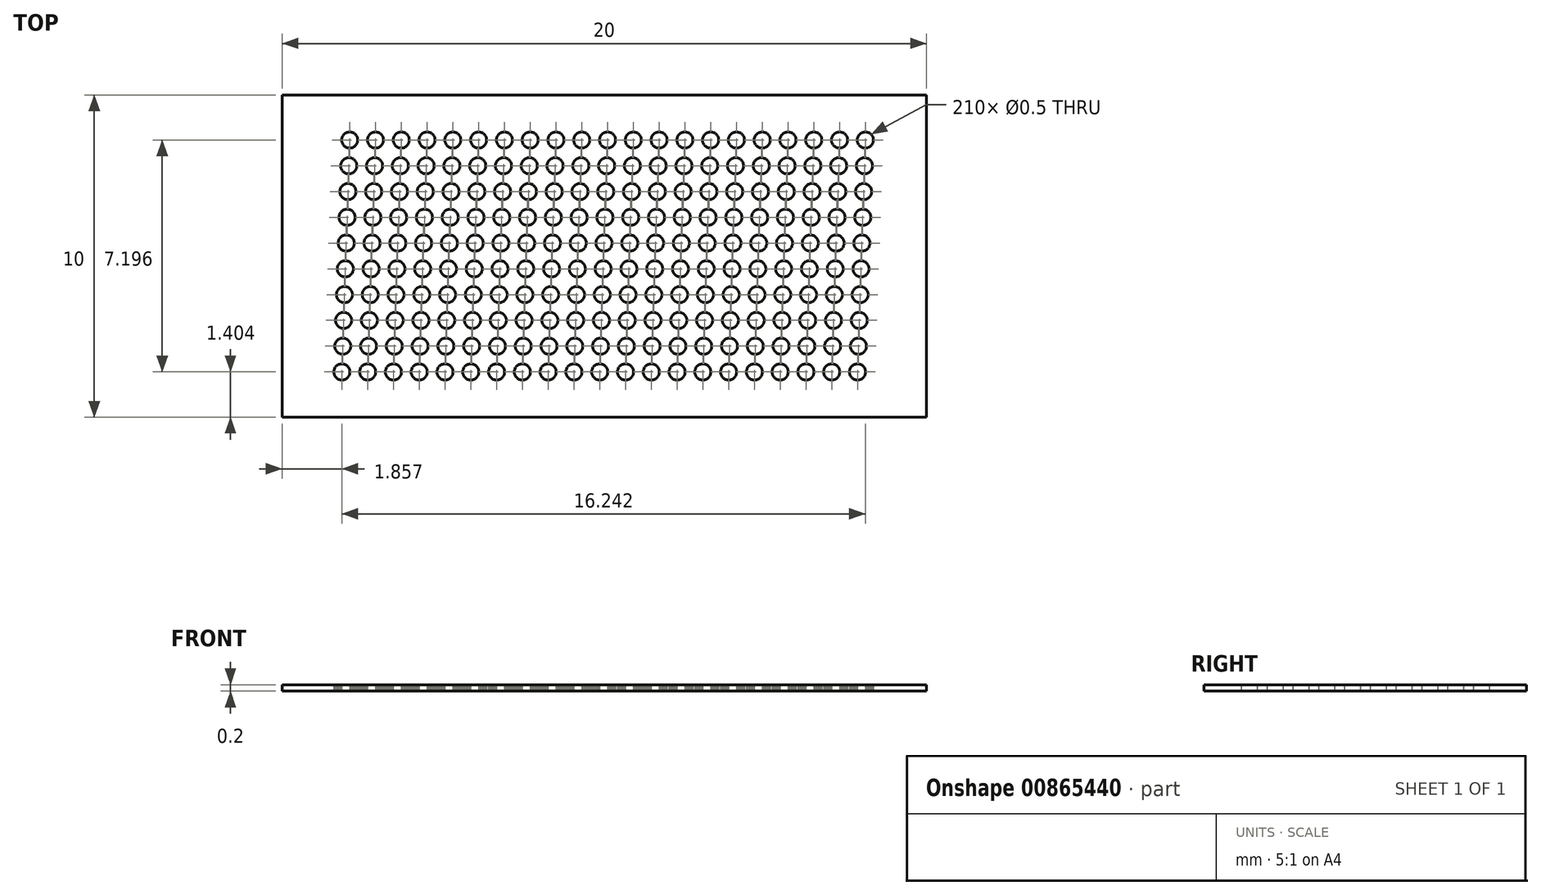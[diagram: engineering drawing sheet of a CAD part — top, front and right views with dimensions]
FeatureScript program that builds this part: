
annotation { "Feature Type Name" : "Feature", "Feature Type Description" : "" }
export const myFeature = defineFeature(function(context is Context, id is Id, definition is map)
    precondition{}
    {
        {
            var Q0;
            Q0=qCreatedBy(makeId("Top.planeOp"),FACE);
            var sketch = newSketch(context, id + "F0", { "sketchPlane" : qUnion([Q0])});
            skLineSegment(sketch, "E0.bottom", {"start": v(0, 0) * mm, "end": v(20, 0) * mm});
            skLineSegment(sketch, "E0.top", {"start": v(0, -10) * mm, "end": v(20, -10) * mm});
            skLineSegment(sketch, "E0.left", {"start": v(0, 0) * mm, "end": v(0, -10) * mm});
            skLineSegment(sketch, "E0.right", {"start": v(20, 0) * mm, "end": v(20, -10) * mm});
            skEllipse(sketch, "E1", {"center": v(2.1, -1.4) * mm, "majorRadius": 0.25 * mm, "minorRadius": 0.25 * mm, "majorAxis": v(0.92, 0.38)});
            skEllipse(sketch, "E2.1.0.0", {"center": v(2.9, -1.4) * mm, "majorRadius": 0.25 * mm, "minorRadius": 0.25 * mm, "majorAxis": v(0.92, 0.38)});
            skEllipse(sketch, "E2.2.0.0", {"center": v(3.7, -1.4) * mm, "majorRadius": 0.25 * mm, "minorRadius": 0.25 * mm, "majorAxis": v(0.92, 0.38)});
            skLineSegment(sketch, "E2.direction1", {"start": v(2.1, -1.4) * mm, "end": v(2.9, -1.4) * mm, "construction": true});
            skEllipse(sketch, "E3.0.3.0", {"center": v(4.5, -1.4) * mm, "majorRadius": 0.25 * mm, "minorRadius": 0.25 * mm, "majorAxis": v(0.92, 0.38)});
            skEllipse(sketch, "E3.0.4.0", {"center": v(5.3, -1.4) * mm, "majorRadius": 0.25 * mm, "minorRadius": 0.25 * mm, "majorAxis": v(0.92, 0.38)});
            skEllipse(sketch, "E3.0.5.0", {"center": v(6.1, -1.4) * mm, "majorRadius": 0.25 * mm, "minorRadius": 0.25 * mm, "majorAxis": v(0.92, 0.38)});
            skEllipse(sketch, "E3.0.6.0", {"center": v(6.9, -1.4) * mm, "majorRadius": 0.25 * mm, "minorRadius": 0.25 * mm, "majorAxis": v(0.92, 0.38)});
            skEllipse(sketch, "E3.0.7.0", {"center": v(7.7, -1.4) * mm, "majorRadius": 0.25 * mm, "minorRadius": 0.25 * mm, "majorAxis": v(0.92, 0.38)});
            skEllipse(sketch, "E3.0.8.0", {"center": v(8.5, -1.4) * mm, "majorRadius": 0.25 * mm, "minorRadius": 0.25 * mm, "majorAxis": v(0.92, 0.38)});
            skEllipse(sketch, "E3.0.9.0", {"center": v(9.3, -1.4) * mm, "majorRadius": 0.25 * mm, "minorRadius": 0.25 * mm, "majorAxis": v(0.92, 0.38)});
            skEllipse(sketch, "E3.0.10.0", {"center": v(10.1, -1.4) * mm, "majorRadius": 0.25 * mm, "minorRadius": 0.25 * mm, "majorAxis": v(0.92, 0.38)});
            skEllipse(sketch, "E3.0.11.0", {"center": v(10.9, -1.4) * mm, "majorRadius": 0.25 * mm, "minorRadius": 0.25 * mm, "majorAxis": v(0.92, 0.38)});
            skEllipse(sketch, "E3.0.12.0", {"center": v(11.7, -1.4) * mm, "majorRadius": 0.25 * mm, "minorRadius": 0.25 * mm, "majorAxis": v(0.92, 0.38)});
            skEllipse(sketch, "E3.0.13.0", {"center": v(12.5, -1.4) * mm, "majorRadius": 0.25 * mm, "minorRadius": 0.25 * mm, "majorAxis": v(0.92, 0.38)});
            skEllipse(sketch, "E3.0.14.0", {"center": v(13.3, -1.4) * mm, "majorRadius": 0.25 * mm, "minorRadius": 0.25 * mm, "majorAxis": v(0.92, 0.38)});
            skEllipse(sketch, "E3.0.15.0", {"center": v(14.1, -1.4) * mm, "majorRadius": 0.25 * mm, "minorRadius": 0.25 * mm, "majorAxis": v(0.92, 0.38)});
            skEllipse(sketch, "E3.0.16.0", {"center": v(14.9, -1.4) * mm, "majorRadius": 0.25 * mm, "minorRadius": 0.25 * mm, "majorAxis": v(0.92, 0.38)});
            skEllipse(sketch, "E3.0.17.0", {"center": v(15.7, -1.4) * mm, "majorRadius": 0.25 * mm, "minorRadius": 0.25 * mm, "majorAxis": v(0.92, 0.38)});
            skEllipse(sketch, "E3.0.18.0", {"center": v(16.5, -1.4) * mm, "majorRadius": 0.25 * mm, "minorRadius": 0.25 * mm, "majorAxis": v(0.92, 0.38)});
            skEllipse(sketch, "E3.0.19.0", {"center": v(17.3, -1.4) * mm, "majorRadius": 0.25 * mm, "minorRadius": 0.25 * mm, "majorAxis": v(0.92, 0.38)});
            skEllipse(sketch, "E4.0.20.0", {"center": v(18.1, -1.4) * mm, "majorRadius": 0.25 * mm, "minorRadius": 0.25 * mm, "majorAxis": v(0.92, 0.38)});
            skEllipse(sketch, "E5.1.0.0", {"center": v(18.07, -2.2) * mm, "majorRadius": 0.25 * mm, "minorRadius": 0.25 * mm, "majorAxis": v(0.92, 0.38)});
            skEllipse(sketch, "E5.1.0.1", {"center": v(17.27, -2.2) * mm, "majorRadius": 0.25 * mm, "minorRadius": 0.25 * mm, "majorAxis": v(0.92, 0.38)});
            skEllipse(sketch, "E5.1.0.2", {"center": v(16.47, -2.2) * mm, "majorRadius": 0.25 * mm, "minorRadius": 0.25 * mm, "majorAxis": v(0.92, 0.38)});
            skEllipse(sketch, "E5.1.0.3", {"center": v(15.67, -2.2) * mm, "majorRadius": 0.25 * mm, "minorRadius": 0.25 * mm, "majorAxis": v(0.92, 0.38)});
            skEllipse(sketch, "E5.1.0.4", {"center": v(14.87, -2.2) * mm, "majorRadius": 0.25 * mm, "minorRadius": 0.25 * mm, "majorAxis": v(0.92, 0.38)});
            skEllipse(sketch, "E5.1.0.5", {"center": v(14.07, -2.2) * mm, "majorRadius": 0.25 * mm, "minorRadius": 0.25 * mm, "majorAxis": v(0.92, 0.38)});
            skEllipse(sketch, "E5.1.0.6", {"center": v(13.27, -2.2) * mm, "majorRadius": 0.25 * mm, "minorRadius": 0.25 * mm, "majorAxis": v(0.92, 0.38)});
            skEllipse(sketch, "E5.1.0.7", {"center": v(12.47, -2.2) * mm, "majorRadius": 0.25 * mm, "minorRadius": 0.25 * mm, "majorAxis": v(0.92, 0.38)});
            skEllipse(sketch, "E5.1.0.8", {"center": v(11.67, -2.2) * mm, "majorRadius": 0.25 * mm, "minorRadius": 0.25 * mm, "majorAxis": v(0.92, 0.38)});
            skEllipse(sketch, "E5.1.0.9", {"center": v(10.87, -2.2) * mm, "majorRadius": 0.25 * mm, "minorRadius": 0.25 * mm, "majorAxis": v(0.92, 0.38)});
            skEllipse(sketch, "E5.1.0.10", {"center": v(10.07, -2.2) * mm, "majorRadius": 0.25 * mm, "minorRadius": 0.25 * mm, "majorAxis": v(0.92, 0.38)});
            skEllipse(sketch, "E5.1.0.11", {"center": v(9.27, -2.2) * mm, "majorRadius": 0.25 * mm, "minorRadius": 0.25 * mm, "majorAxis": v(0.92, 0.38)});
            skEllipse(sketch, "E5.1.0.12", {"center": v(8.47, -2.2) * mm, "majorRadius": 0.25 * mm, "minorRadius": 0.25 * mm, "majorAxis": v(0.92, 0.38)});
            skEllipse(sketch, "E5.1.0.13", {"center": v(7.67, -2.2) * mm, "majorRadius": 0.25 * mm, "minorRadius": 0.25 * mm, "majorAxis": v(0.92, 0.38)});
            skEllipse(sketch, "E5.1.0.14", {"center": v(6.87, -2.2) * mm, "majorRadius": 0.25 * mm, "minorRadius": 0.25 * mm, "majorAxis": v(0.92, 0.38)});
            skEllipse(sketch, "E5.1.0.15", {"center": v(5.27, -2.2) * mm, "majorRadius": 0.25 * mm, "minorRadius": 0.25 * mm, "majorAxis": v(0.92, 0.38)});
            skEllipse(sketch, "E5.1.0.16", {"center": v(4.47, -2.2) * mm, "majorRadius": 0.25 * mm, "minorRadius": 0.25 * mm, "majorAxis": v(0.92, 0.38)});
            skEllipse(sketch, "E5.1.0.17", {"center": v(6.07, -2.2) * mm, "majorRadius": 0.25 * mm, "minorRadius": 0.25 * mm, "majorAxis": v(0.92, 0.38)});
            skEllipse(sketch, "E5.1.0.18", {"center": v(3.67, -2.2) * mm, "majorRadius": 0.25 * mm, "minorRadius": 0.25 * mm, "majorAxis": v(0.92, 0.38)});
            skEllipse(sketch, "E5.1.0.19", {"center": v(2.87, -2.2) * mm, "majorRadius": 0.25 * mm, "minorRadius": 0.25 * mm, "majorAxis": v(0.92, 0.38)});
            skEllipse(sketch, "E5.1.0.20", {"center": v(2.07, -2.2) * mm, "majorRadius": 0.25 * mm, "minorRadius": 0.25 * mm, "majorAxis": v(0.92, 0.38)});
            skEllipse(sketch, "E5.2.0.0", {"center": v(18.05, -3) * mm, "majorRadius": 0.25 * mm, "minorRadius": 0.25 * mm, "majorAxis": v(0.92, 0.38)});
            skEllipse(sketch, "E5.2.0.1", {"center": v(17.25, -3) * mm, "majorRadius": 0.25 * mm, "minorRadius": 0.25 * mm, "majorAxis": v(0.92, 0.38)});
            skEllipse(sketch, "E5.2.0.2", {"center": v(16.45, -3) * mm, "majorRadius": 0.25 * mm, "minorRadius": 0.25 * mm, "majorAxis": v(0.92, 0.38)});
            skEllipse(sketch, "E5.2.0.3", {"center": v(15.65, -3) * mm, "majorRadius": 0.25 * mm, "minorRadius": 0.25 * mm, "majorAxis": v(0.92, 0.38)});
            skEllipse(sketch, "E5.2.0.4", {"center": v(14.85, -3) * mm, "majorRadius": 0.25 * mm, "minorRadius": 0.25 * mm, "majorAxis": v(0.92, 0.38)});
            skEllipse(sketch, "E5.2.0.5", {"center": v(14.05, -3) * mm, "majorRadius": 0.25 * mm, "minorRadius": 0.25 * mm, "majorAxis": v(0.92, 0.38)});
            skEllipse(sketch, "E5.2.0.6", {"center": v(13.25, -3) * mm, "majorRadius": 0.25 * mm, "minorRadius": 0.25 * mm, "majorAxis": v(0.92, 0.38)});
            skEllipse(sketch, "E5.2.0.7", {"center": v(12.45, -3) * mm, "majorRadius": 0.25 * mm, "minorRadius": 0.25 * mm, "majorAxis": v(0.92, 0.38)});
            skEllipse(sketch, "E5.2.0.8", {"center": v(11.65, -3) * mm, "majorRadius": 0.25 * mm, "minorRadius": 0.25 * mm, "majorAxis": v(0.92, 0.38)});
            skEllipse(sketch, "E5.2.0.9", {"center": v(10.85, -3) * mm, "majorRadius": 0.25 * mm, "minorRadius": 0.25 * mm, "majorAxis": v(0.92, 0.38)});
            skEllipse(sketch, "E5.2.0.10", {"center": v(10.05, -3) * mm, "majorRadius": 0.25 * mm, "minorRadius": 0.25 * mm, "majorAxis": v(0.92, 0.38)});
            skEllipse(sketch, "E5.2.0.11", {"center": v(9.25, -3) * mm, "majorRadius": 0.25 * mm, "minorRadius": 0.25 * mm, "majorAxis": v(0.92, 0.38)});
            skEllipse(sketch, "E5.2.0.12", {"center": v(8.45, -3) * mm, "majorRadius": 0.25 * mm, "minorRadius": 0.25 * mm, "majorAxis": v(0.92, 0.38)});
            skEllipse(sketch, "E5.2.0.13", {"center": v(7.65, -3) * mm, "majorRadius": 0.25 * mm, "minorRadius": 0.25 * mm, "majorAxis": v(0.92, 0.38)});
            skEllipse(sketch, "E5.2.0.14", {"center": v(6.85, -3) * mm, "majorRadius": 0.25 * mm, "minorRadius": 0.25 * mm, "majorAxis": v(0.92, 0.38)});
            skEllipse(sketch, "E5.2.0.15", {"center": v(5.25, -3) * mm, "majorRadius": 0.25 * mm, "minorRadius": 0.25 * mm, "majorAxis": v(0.92, 0.38)});
            skEllipse(sketch, "E5.2.0.16", {"center": v(4.45, -3) * mm, "majorRadius": 0.25 * mm, "minorRadius": 0.25 * mm, "majorAxis": v(0.92, 0.38)});
            skEllipse(sketch, "E5.2.0.17", {"center": v(6.05, -3) * mm, "majorRadius": 0.25 * mm, "minorRadius": 0.25 * mm, "majorAxis": v(0.92, 0.38)});
            skEllipse(sketch, "E5.2.0.18", {"center": v(3.65, -3) * mm, "majorRadius": 0.25 * mm, "minorRadius": 0.25 * mm, "majorAxis": v(0.92, 0.38)});
            skEllipse(sketch, "E5.2.0.19", {"center": v(2.85, -3) * mm, "majorRadius": 0.25 * mm, "minorRadius": 0.25 * mm, "majorAxis": v(0.92, 0.38)});
            skEllipse(sketch, "E5.2.0.20", {"center": v(2.05, -3) * mm, "majorRadius": 0.25 * mm, "minorRadius": 0.25 * mm, "majorAxis": v(0.92, 0.38)});
            skEllipse(sketch, "E5.3.0.0", {"center": v(18.02, -3.8) * mm, "majorRadius": 0.25 * mm, "minorRadius": 0.25 * mm, "majorAxis": v(0.92, 0.38)});
            skEllipse(sketch, "E5.3.0.1", {"center": v(17.22, -3.8) * mm, "majorRadius": 0.25 * mm, "minorRadius": 0.25 * mm, "majorAxis": v(0.92, 0.38)});
            skEllipse(sketch, "E5.3.0.2", {"center": v(16.42, -3.8) * mm, "majorRadius": 0.25 * mm, "minorRadius": 0.25 * mm, "majorAxis": v(0.92, 0.38)});
            skEllipse(sketch, "E5.3.0.3", {"center": v(15.62, -3.8) * mm, "majorRadius": 0.25 * mm, "minorRadius": 0.25 * mm, "majorAxis": v(0.92, 0.38)});
            skEllipse(sketch, "E5.3.0.4", {"center": v(14.82, -3.8) * mm, "majorRadius": 0.25 * mm, "minorRadius": 0.25 * mm, "majorAxis": v(0.92, 0.38)});
            skEllipse(sketch, "E5.3.0.5", {"center": v(14.02, -3.8) * mm, "majorRadius": 0.25 * mm, "minorRadius": 0.25 * mm, "majorAxis": v(0.92, 0.38)});
            skEllipse(sketch, "E5.3.0.6", {"center": v(13.22, -3.8) * mm, "majorRadius": 0.25 * mm, "minorRadius": 0.25 * mm, "majorAxis": v(0.92, 0.38)});
            skEllipse(sketch, "E5.3.0.7", {"center": v(12.42, -3.8) * mm, "majorRadius": 0.25 * mm, "minorRadius": 0.25 * mm, "majorAxis": v(0.92, 0.38)});
            skEllipse(sketch, "E5.3.0.8", {"center": v(11.62, -3.8) * mm, "majorRadius": 0.25 * mm, "minorRadius": 0.25 * mm, "majorAxis": v(0.92, 0.38)});
            skEllipse(sketch, "E5.3.0.9", {"center": v(10.82, -3.8) * mm, "majorRadius": 0.25 * mm, "minorRadius": 0.25 * mm, "majorAxis": v(0.92, 0.38)});
            skEllipse(sketch, "E5.3.0.10", {"center": v(10.02, -3.8) * mm, "majorRadius": 0.25 * mm, "minorRadius": 0.25 * mm, "majorAxis": v(0.92, 0.38)});
            skEllipse(sketch, "E5.3.0.11", {"center": v(9.22, -3.8) * mm, "majorRadius": 0.25 * mm, "minorRadius": 0.25 * mm, "majorAxis": v(0.92, 0.38)});
            skEllipse(sketch, "E5.3.0.12", {"center": v(8.42, -3.8) * mm, "majorRadius": 0.25 * mm, "minorRadius": 0.25 * mm, "majorAxis": v(0.92, 0.38)});
            skEllipse(sketch, "E5.3.0.13", {"center": v(7.62, -3.8) * mm, "majorRadius": 0.25 * mm, "minorRadius": 0.25 * mm, "majorAxis": v(0.92, 0.38)});
            skEllipse(sketch, "E5.3.0.14", {"center": v(6.82, -3.8) * mm, "majorRadius": 0.25 * mm, "minorRadius": 0.25 * mm, "majorAxis": v(0.92, 0.38)});
            skEllipse(sketch, "E5.3.0.15", {"center": v(5.22, -3.8) * mm, "majorRadius": 0.25 * mm, "minorRadius": 0.25 * mm, "majorAxis": v(0.92, 0.38)});
            skEllipse(sketch, "E5.3.0.16", {"center": v(4.42, -3.8) * mm, "majorRadius": 0.25 * mm, "minorRadius": 0.25 * mm, "majorAxis": v(0.92, 0.38)});
            skEllipse(sketch, "E5.3.0.17", {"center": v(6.02, -3.8) * mm, "majorRadius": 0.25 * mm, "minorRadius": 0.25 * mm, "majorAxis": v(0.92, 0.38)});
            skEllipse(sketch, "E5.3.0.18", {"center": v(3.62, -3.8) * mm, "majorRadius": 0.25 * mm, "minorRadius": 0.25 * mm, "majorAxis": v(0.92, 0.38)});
            skEllipse(sketch, "E5.3.0.19", {"center": v(2.82, -3.8) * mm, "majorRadius": 0.25 * mm, "minorRadius": 0.25 * mm, "majorAxis": v(0.92, 0.38)});
            skEllipse(sketch, "E5.3.0.20", {"center": v(2.02, -3.8) * mm, "majorRadius": 0.25 * mm, "minorRadius": 0.25 * mm, "majorAxis": v(0.92, 0.38)});
            skEllipse(sketch, "E5.4.0.0", {"center": v(18, -4.6) * mm, "majorRadius": 0.25 * mm, "minorRadius": 0.25 * mm, "majorAxis": v(0.92, 0.38)});
            skEllipse(sketch, "E5.4.0.1", {"center": v(17.2, -4.6) * mm, "majorRadius": 0.25 * mm, "minorRadius": 0.25 * mm, "majorAxis": v(0.92, 0.38)});
            skEllipse(sketch, "E5.4.0.2", {"center": v(16.4, -4.6) * mm, "majorRadius": 0.25 * mm, "minorRadius": 0.25 * mm, "majorAxis": v(0.92, 0.38)});
            skEllipse(sketch, "E5.4.0.3", {"center": v(15.6, -4.6) * mm, "majorRadius": 0.25 * mm, "minorRadius": 0.25 * mm, "majorAxis": v(0.92, 0.38)});
            skEllipse(sketch, "E5.4.0.4", {"center": v(14.8, -4.6) * mm, "majorRadius": 0.25 * mm, "minorRadius": 0.25 * mm, "majorAxis": v(0.92, 0.38)});
            skEllipse(sketch, "E5.4.0.5", {"center": v(14, -4.6) * mm, "majorRadius": 0.25 * mm, "minorRadius": 0.25 * mm, "majorAxis": v(0.92, 0.38)});
            skEllipse(sketch, "E5.4.0.6", {"center": v(13.2, -4.6) * mm, "majorRadius": 0.25 * mm, "minorRadius": 0.25 * mm, "majorAxis": v(0.92, 0.38)});
            skEllipse(sketch, "E5.4.0.7", {"center": v(12.4, -4.6) * mm, "majorRadius": 0.25 * mm, "minorRadius": 0.25 * mm, "majorAxis": v(0.92, 0.38)});
            skEllipse(sketch, "E5.4.0.8", {"center": v(11.6, -4.6) * mm, "majorRadius": 0.25 * mm, "minorRadius": 0.25 * mm, "majorAxis": v(0.92, 0.38)});
            skEllipse(sketch, "E5.4.0.9", {"center": v(10.8, -4.6) * mm, "majorRadius": 0.25 * mm, "minorRadius": 0.25 * mm, "majorAxis": v(0.92, 0.38)});
            skEllipse(sketch, "E5.4.0.10", {"center": v(10, -4.6) * mm, "majorRadius": 0.25 * mm, "minorRadius": 0.25 * mm, "majorAxis": v(0.92, 0.38)});
            skEllipse(sketch, "E5.4.0.11", {"center": v(9.2, -4.6) * mm, "majorRadius": 0.25 * mm, "minorRadius": 0.25 * mm, "majorAxis": v(0.92, 0.38)});
            skEllipse(sketch, "E5.4.0.12", {"center": v(8.4, -4.6) * mm, "majorRadius": 0.25 * mm, "minorRadius": 0.25 * mm, "majorAxis": v(0.92, 0.38)});
            skEllipse(sketch, "E5.4.0.13", {"center": v(7.6, -4.6) * mm, "majorRadius": 0.25 * mm, "minorRadius": 0.25 * mm, "majorAxis": v(0.92, 0.38)});
            skEllipse(sketch, "E5.4.0.14", {"center": v(6.8, -4.6) * mm, "majorRadius": 0.25 * mm, "minorRadius": 0.25 * mm, "majorAxis": v(0.92, 0.38)});
            skEllipse(sketch, "E5.4.0.15", {"center": v(5.2, -4.6) * mm, "majorRadius": 0.25 * mm, "minorRadius": 0.25 * mm, "majorAxis": v(0.92, 0.38)});
            skEllipse(sketch, "E5.4.0.16", {"center": v(4.4, -4.6) * mm, "majorRadius": 0.25 * mm, "minorRadius": 0.25 * mm, "majorAxis": v(0.92, 0.38)});
            skEllipse(sketch, "E5.4.0.17", {"center": v(6, -4.6) * mm, "majorRadius": 0.25 * mm, "minorRadius": 0.25 * mm, "majorAxis": v(0.92, 0.38)});
            skEllipse(sketch, "E5.4.0.18", {"center": v(3.6, -4.6) * mm, "majorRadius": 0.25 * mm, "minorRadius": 0.25 * mm, "majorAxis": v(0.92, 0.38)});
            skEllipse(sketch, "E5.4.0.19", {"center": v(2.8, -4.6) * mm, "majorRadius": 0.25 * mm, "minorRadius": 0.25 * mm, "majorAxis": v(0.92, 0.38)});
            skEllipse(sketch, "E5.4.0.20", {"center": v(2, -4.6) * mm, "majorRadius": 0.25 * mm, "minorRadius": 0.25 * mm, "majorAxis": v(0.92, 0.38)});
            skEllipse(sketch, "E5.5.0.0", {"center": v(17.97, -5.4) * mm, "majorRadius": 0.25 * mm, "minorRadius": 0.25 * mm, "majorAxis": v(0.92, 0.38)});
            skEllipse(sketch, "E5.5.0.1", {"center": v(17.17, -5.4) * mm, "majorRadius": 0.25 * mm, "minorRadius": 0.25 * mm, "majorAxis": v(0.92, 0.38)});
            skEllipse(sketch, "E5.5.0.2", {"center": v(16.37, -5.4) * mm, "majorRadius": 0.25 * mm, "minorRadius": 0.25 * mm, "majorAxis": v(0.92, 0.38)});
            skEllipse(sketch, "E5.5.0.3", {"center": v(15.57, -5.4) * mm, "majorRadius": 0.25 * mm, "minorRadius": 0.25 * mm, "majorAxis": v(0.92, 0.38)});
            skEllipse(sketch, "E5.5.0.4", {"center": v(14.77, -5.4) * mm, "majorRadius": 0.25 * mm, "minorRadius": 0.25 * mm, "majorAxis": v(0.92, 0.38)});
            skEllipse(sketch, "E5.5.0.5", {"center": v(13.97, -5.4) * mm, "majorRadius": 0.25 * mm, "minorRadius": 0.25 * mm, "majorAxis": v(0.92, 0.38)});
            skEllipse(sketch, "E5.5.0.6", {"center": v(13.17, -5.4) * mm, "majorRadius": 0.25 * mm, "minorRadius": 0.25 * mm, "majorAxis": v(0.92, 0.38)});
            skEllipse(sketch, "E5.5.0.7", {"center": v(12.37, -5.4) * mm, "majorRadius": 0.25 * mm, "minorRadius": 0.25 * mm, "majorAxis": v(0.92, 0.38)});
            skEllipse(sketch, "E5.5.0.8", {"center": v(11.57, -5.4) * mm, "majorRadius": 0.25 * mm, "minorRadius": 0.25 * mm, "majorAxis": v(0.92, 0.38)});
            skEllipse(sketch, "E5.5.0.9", {"center": v(10.77, -5.4) * mm, "majorRadius": 0.25 * mm, "minorRadius": 0.25 * mm, "majorAxis": v(0.92, 0.38)});
            skEllipse(sketch, "E5.5.0.10", {"center": v(9.97, -5.4) * mm, "majorRadius": 0.25 * mm, "minorRadius": 0.25 * mm, "majorAxis": v(0.92, 0.38)});
            skEllipse(sketch, "E5.5.0.11", {"center": v(9.17, -5.4) * mm, "majorRadius": 0.25 * mm, "minorRadius": 0.25 * mm, "majorAxis": v(0.92, 0.38)});
            skEllipse(sketch, "E5.5.0.12", {"center": v(8.37, -5.4) * mm, "majorRadius": 0.25 * mm, "minorRadius": 0.25 * mm, "majorAxis": v(0.92, 0.38)});
            skEllipse(sketch, "E5.5.0.13", {"center": v(7.57, -5.4) * mm, "majorRadius": 0.25 * mm, "minorRadius": 0.25 * mm, "majorAxis": v(0.92, 0.38)});
            skEllipse(sketch, "E5.5.0.14", {"center": v(6.77, -5.4) * mm, "majorRadius": 0.25 * mm, "minorRadius": 0.25 * mm, "majorAxis": v(0.92, 0.38)});
            skEllipse(sketch, "E5.5.0.15", {"center": v(5.17, -5.4) * mm, "majorRadius": 0.25 * mm, "minorRadius": 0.25 * mm, "majorAxis": v(0.92, 0.38)});
            skEllipse(sketch, "E5.5.0.16", {"center": v(4.37, -5.4) * mm, "majorRadius": 0.25 * mm, "minorRadius": 0.25 * mm, "majorAxis": v(0.92, 0.38)});
            skEllipse(sketch, "E5.5.0.17", {"center": v(5.97, -5.4) * mm, "majorRadius": 0.25 * mm, "minorRadius": 0.25 * mm, "majorAxis": v(0.92, 0.38)});
            skEllipse(sketch, "E5.5.0.18", {"center": v(3.57, -5.4) * mm, "majorRadius": 0.25 * mm, "minorRadius": 0.25 * mm, "majorAxis": v(0.92, 0.38)});
            skEllipse(sketch, "E5.5.0.19", {"center": v(2.77, -5.4) * mm, "majorRadius": 0.25 * mm, "minorRadius": 0.25 * mm, "majorAxis": v(0.92, 0.38)});
            skEllipse(sketch, "E5.5.0.20", {"center": v(1.97, -5.4) * mm, "majorRadius": 0.25 * mm, "minorRadius": 0.25 * mm, "majorAxis": v(0.92, 0.38)});
            skEllipse(sketch, "E5.6.0.0", {"center": v(17.94, -6.2) * mm, "majorRadius": 0.25 * mm, "minorRadius": 0.25 * mm, "majorAxis": v(0.92, 0.38)});
            skEllipse(sketch, "E5.6.0.1", {"center": v(17.14, -6.2) * mm, "majorRadius": 0.25 * mm, "minorRadius": 0.25 * mm, "majorAxis": v(0.92, 0.38)});
            skEllipse(sketch, "E5.6.0.2", {"center": v(16.34, -6.2) * mm, "majorRadius": 0.25 * mm, "minorRadius": 0.25 * mm, "majorAxis": v(0.92, 0.38)});
            skEllipse(sketch, "E5.6.0.3", {"center": v(15.54, -6.2) * mm, "majorRadius": 0.25 * mm, "minorRadius": 0.25 * mm, "majorAxis": v(0.92, 0.38)});
            skEllipse(sketch, "E5.6.0.4", {"center": v(14.74, -6.2) * mm, "majorRadius": 0.25 * mm, "minorRadius": 0.25 * mm, "majorAxis": v(0.92, 0.38)});
            skEllipse(sketch, "E5.6.0.5", {"center": v(13.94, -6.2) * mm, "majorRadius": 0.25 * mm, "minorRadius": 0.25 * mm, "majorAxis": v(0.92, 0.38)});
            skEllipse(sketch, "E5.6.0.6", {"center": v(13.14, -6.2) * mm, "majorRadius": 0.25 * mm, "minorRadius": 0.25 * mm, "majorAxis": v(0.92, 0.38)});
            skEllipse(sketch, "E5.6.0.7", {"center": v(12.34, -6.2) * mm, "majorRadius": 0.25 * mm, "minorRadius": 0.25 * mm, "majorAxis": v(0.92, 0.38)});
            skEllipse(sketch, "E5.6.0.8", {"center": v(11.54, -6.2) * mm, "majorRadius": 0.25 * mm, "minorRadius": 0.25 * mm, "majorAxis": v(0.92, 0.38)});
            skEllipse(sketch, "E5.6.0.9", {"center": v(10.74, -6.2) * mm, "majorRadius": 0.25 * mm, "minorRadius": 0.25 * mm, "majorAxis": v(0.92, 0.38)});
            skEllipse(sketch, "E5.6.0.10", {"center": v(9.94, -6.2) * mm, "majorRadius": 0.25 * mm, "minorRadius": 0.25 * mm, "majorAxis": v(0.92, 0.38)});
            skEllipse(sketch, "E5.6.0.11", {"center": v(9.14, -6.2) * mm, "majorRadius": 0.25 * mm, "minorRadius": 0.25 * mm, "majorAxis": v(0.92, 0.38)});
            skEllipse(sketch, "E5.6.0.12", {"center": v(8.34, -6.2) * mm, "majorRadius": 0.25 * mm, "minorRadius": 0.25 * mm, "majorAxis": v(0.92, 0.38)});
            skEllipse(sketch, "E5.6.0.13", {"center": v(7.54, -6.2) * mm, "majorRadius": 0.25 * mm, "minorRadius": 0.25 * mm, "majorAxis": v(0.92, 0.38)});
            skEllipse(sketch, "E5.6.0.14", {"center": v(6.74, -6.2) * mm, "majorRadius": 0.25 * mm, "minorRadius": 0.25 * mm, "majorAxis": v(0.92, 0.38)});
            skEllipse(sketch, "E5.6.0.15", {"center": v(5.14, -6.2) * mm, "majorRadius": 0.25 * mm, "minorRadius": 0.25 * mm, "majorAxis": v(0.92, 0.38)});
            skEllipse(sketch, "E5.6.0.16", {"center": v(4.34, -6.2) * mm, "majorRadius": 0.25 * mm, "minorRadius": 0.25 * mm, "majorAxis": v(0.92, 0.38)});
            skEllipse(sketch, "E5.6.0.17", {"center": v(5.94, -6.2) * mm, "majorRadius": 0.25 * mm, "minorRadius": 0.25 * mm, "majorAxis": v(0.92, 0.38)});
            skEllipse(sketch, "E5.6.0.18", {"center": v(3.54, -6.2) * mm, "majorRadius": 0.25 * mm, "minorRadius": 0.25 * mm, "majorAxis": v(0.92, 0.38)});
            skEllipse(sketch, "E5.6.0.19", {"center": v(2.74, -6.2) * mm, "majorRadius": 0.25 * mm, "minorRadius": 0.25 * mm, "majorAxis": v(0.92, 0.38)});
            skEllipse(sketch, "E5.6.0.20", {"center": v(1.94, -6.2) * mm, "majorRadius": 0.25 * mm, "minorRadius": 0.25 * mm, "majorAxis": v(0.92, 0.38)});
            skEllipse(sketch, "E5.7.0.0", {"center": v(17.91, -7) * mm, "majorRadius": 0.25 * mm, "minorRadius": 0.25 * mm, "majorAxis": v(0.92, 0.38)});
            skEllipse(sketch, "E5.7.0.1", {"center": v(17.11, -7) * mm, "majorRadius": 0.25 * mm, "minorRadius": 0.25 * mm, "majorAxis": v(0.92, 0.38)});
            skEllipse(sketch, "E5.7.0.2", {"center": v(16.31, -7) * mm, "majorRadius": 0.25 * mm, "minorRadius": 0.25 * mm, "majorAxis": v(0.92, 0.38)});
            skEllipse(sketch, "E5.7.0.3", {"center": v(15.51, -7) * mm, "majorRadius": 0.25 * mm, "minorRadius": 0.25 * mm, "majorAxis": v(0.92, 0.38)});
            skEllipse(sketch, "E5.7.0.4", {"center": v(14.71, -7) * mm, "majorRadius": 0.25 * mm, "minorRadius": 0.25 * mm, "majorAxis": v(0.92, 0.38)});
            skEllipse(sketch, "E5.7.0.5", {"center": v(13.91, -7) * mm, "majorRadius": 0.25 * mm, "minorRadius": 0.25 * mm, "majorAxis": v(0.92, 0.38)});
            skEllipse(sketch, "E5.7.0.6", {"center": v(13.11, -7) * mm, "majorRadius": 0.25 * mm, "minorRadius": 0.25 * mm, "majorAxis": v(0.92, 0.38)});
            skEllipse(sketch, "E5.7.0.7", {"center": v(12.31, -7) * mm, "majorRadius": 0.25 * mm, "minorRadius": 0.25 * mm, "majorAxis": v(0.92, 0.38)});
            skEllipse(sketch, "E5.7.0.8", {"center": v(11.51, -7) * mm, "majorRadius": 0.25 * mm, "minorRadius": 0.25 * mm, "majorAxis": v(0.92, 0.38)});
            skEllipse(sketch, "E5.7.0.9", {"center": v(10.71, -7) * mm, "majorRadius": 0.25 * mm, "minorRadius": 0.25 * mm, "majorAxis": v(0.92, 0.38)});
            skEllipse(sketch, "E5.7.0.10", {"center": v(9.91, -7) * mm, "majorRadius": 0.25 * mm, "minorRadius": 0.25 * mm, "majorAxis": v(0.92, 0.38)});
            skEllipse(sketch, "E5.7.0.11", {"center": v(9.11, -7) * mm, "majorRadius": 0.25 * mm, "minorRadius": 0.25 * mm, "majorAxis": v(0.92, 0.38)});
            skEllipse(sketch, "E5.7.0.12", {"center": v(8.31, -7) * mm, "majorRadius": 0.25 * mm, "minorRadius": 0.25 * mm, "majorAxis": v(0.92, 0.38)});
            skEllipse(sketch, "E5.7.0.13", {"center": v(7.51, -7) * mm, "majorRadius": 0.25 * mm, "minorRadius": 0.25 * mm, "majorAxis": v(0.92, 0.38)});
            skEllipse(sketch, "E5.7.0.14", {"center": v(6.71, -7) * mm, "majorRadius": 0.25 * mm, "minorRadius": 0.25 * mm, "majorAxis": v(0.92, 0.38)});
            skEllipse(sketch, "E5.7.0.15", {"center": v(5.11, -7) * mm, "majorRadius": 0.25 * mm, "minorRadius": 0.25 * mm, "majorAxis": v(0.92, 0.38)});
            skEllipse(sketch, "E5.7.0.16", {"center": v(4.31, -7) * mm, "majorRadius": 0.25 * mm, "minorRadius": 0.25 * mm, "majorAxis": v(0.92, 0.38)});
            skEllipse(sketch, "E5.7.0.17", {"center": v(5.91, -7) * mm, "majorRadius": 0.25 * mm, "minorRadius": 0.25 * mm, "majorAxis": v(0.92, 0.38)});
            skEllipse(sketch, "E5.7.0.18", {"center": v(3.51, -7) * mm, "majorRadius": 0.25 * mm, "minorRadius": 0.25 * mm, "majorAxis": v(0.92, 0.38)});
            skEllipse(sketch, "E5.7.0.19", {"center": v(2.71, -7) * mm, "majorRadius": 0.25 * mm, "minorRadius": 0.25 * mm, "majorAxis": v(0.92, 0.38)});
            skEllipse(sketch, "E5.7.0.20", {"center": v(1.91, -7) * mm, "majorRadius": 0.25 * mm, "minorRadius": 0.25 * mm, "majorAxis": v(0.92, 0.38)});
            skEllipse(sketch, "E5.8.0.0", {"center": v(17.88, -7.8) * mm, "majorRadius": 0.25 * mm, "minorRadius": 0.25 * mm, "majorAxis": v(0.92, 0.38)});
            skEllipse(sketch, "E5.8.0.1", {"center": v(17.08, -7.8) * mm, "majorRadius": 0.25 * mm, "minorRadius": 0.25 * mm, "majorAxis": v(0.92, 0.38)});
            skEllipse(sketch, "E5.8.0.2", {"center": v(16.28, -7.8) * mm, "majorRadius": 0.25 * mm, "minorRadius": 0.25 * mm, "majorAxis": v(0.92, 0.38)});
            skEllipse(sketch, "E5.8.0.3", {"center": v(15.48, -7.8) * mm, "majorRadius": 0.25 * mm, "minorRadius": 0.25 * mm, "majorAxis": v(0.92, 0.38)});
            skEllipse(sketch, "E5.8.0.4", {"center": v(14.68, -7.8) * mm, "majorRadius": 0.25 * mm, "minorRadius": 0.25 * mm, "majorAxis": v(0.92, 0.38)});
            skEllipse(sketch, "E5.8.0.5", {"center": v(13.88, -7.8) * mm, "majorRadius": 0.25 * mm, "minorRadius": 0.25 * mm, "majorAxis": v(0.92, 0.38)});
            skEllipse(sketch, "E5.8.0.6", {"center": v(13.08, -7.8) * mm, "majorRadius": 0.25 * mm, "minorRadius": 0.25 * mm, "majorAxis": v(0.92, 0.38)});
            skEllipse(sketch, "E5.8.0.7", {"center": v(12.28, -7.8) * mm, "majorRadius": 0.25 * mm, "minorRadius": 0.25 * mm, "majorAxis": v(0.92, 0.38)});
            skEllipse(sketch, "E5.8.0.8", {"center": v(11.48, -7.8) * mm, "majorRadius": 0.25 * mm, "minorRadius": 0.25 * mm, "majorAxis": v(0.92, 0.38)});
            skEllipse(sketch, "E5.8.0.9", {"center": v(10.68, -7.8) * mm, "majorRadius": 0.25 * mm, "minorRadius": 0.25 * mm, "majorAxis": v(0.92, 0.38)});
            skEllipse(sketch, "E5.8.0.10", {"center": v(9.88, -7.8) * mm, "majorRadius": 0.25 * mm, "minorRadius": 0.25 * mm, "majorAxis": v(0.92, 0.38)});
            skEllipse(sketch, "E5.8.0.11", {"center": v(9.08, -7.8) * mm, "majorRadius": 0.25 * mm, "minorRadius": 0.25 * mm, "majorAxis": v(0.92, 0.38)});
            skEllipse(sketch, "E5.8.0.12", {"center": v(8.28, -7.8) * mm, "majorRadius": 0.25 * mm, "minorRadius": 0.25 * mm, "majorAxis": v(0.92, 0.38)});
            skEllipse(sketch, "E5.8.0.13", {"center": v(7.48, -7.8) * mm, "majorRadius": 0.25 * mm, "minorRadius": 0.25 * mm, "majorAxis": v(0.92, 0.38)});
            skEllipse(sketch, "E5.8.0.14", {"center": v(6.68, -7.8) * mm, "majorRadius": 0.25 * mm, "minorRadius": 0.25 * mm, "majorAxis": v(0.92, 0.38)});
            skEllipse(sketch, "E5.8.0.15", {"center": v(5.08, -7.8) * mm, "majorRadius": 0.25 * mm, "minorRadius": 0.25 * mm, "majorAxis": v(0.92, 0.38)});
            skEllipse(sketch, "E5.8.0.16", {"center": v(4.28, -7.8) * mm, "majorRadius": 0.25 * mm, "minorRadius": 0.25 * mm, "majorAxis": v(0.92, 0.38)});
            skEllipse(sketch, "E5.8.0.17", {"center": v(5.88, -7.8) * mm, "majorRadius": 0.25 * mm, "minorRadius": 0.25 * mm, "majorAxis": v(0.92, 0.38)});
            skEllipse(sketch, "E5.8.0.18", {"center": v(3.48, -7.8) * mm, "majorRadius": 0.25 * mm, "minorRadius": 0.25 * mm, "majorAxis": v(0.92, 0.38)});
            skEllipse(sketch, "E5.8.0.19", {"center": v(2.68, -7.8) * mm, "majorRadius": 0.25 * mm, "minorRadius": 0.25 * mm, "majorAxis": v(0.92, 0.38)});
            skEllipse(sketch, "E5.8.0.20", {"center": v(1.88, -7.8) * mm, "majorRadius": 0.25 * mm, "minorRadius": 0.25 * mm, "majorAxis": v(0.92, 0.38)});
            skEllipse(sketch, "E5.9.0.0", {"center": v(17.86, -8.6) * mm, "majorRadius": 0.25 * mm, "minorRadius": 0.25 * mm, "majorAxis": v(0.92, 0.38)});
            skEllipse(sketch, "E5.9.0.1", {"center": v(17.06, -8.6) * mm, "majorRadius": 0.25 * mm, "minorRadius": 0.25 * mm, "majorAxis": v(0.92, 0.38)});
            skEllipse(sketch, "E5.9.0.2", {"center": v(16.26, -8.6) * mm, "majorRadius": 0.25 * mm, "minorRadius": 0.25 * mm, "majorAxis": v(0.92, 0.38)});
            skEllipse(sketch, "E5.9.0.3", {"center": v(15.46, -8.6) * mm, "majorRadius": 0.25 * mm, "minorRadius": 0.25 * mm, "majorAxis": v(0.92, 0.38)});
            skEllipse(sketch, "E5.9.0.4", {"center": v(14.66, -8.6) * mm, "majorRadius": 0.25 * mm, "minorRadius": 0.25 * mm, "majorAxis": v(0.92, 0.38)});
            skEllipse(sketch, "E5.9.0.5", {"center": v(13.86, -8.6) * mm, "majorRadius": 0.25 * mm, "minorRadius": 0.25 * mm, "majorAxis": v(0.92, 0.38)});
            skEllipse(sketch, "E5.9.0.6", {"center": v(13.06, -8.6) * mm, "majorRadius": 0.25 * mm, "minorRadius": 0.25 * mm, "majorAxis": v(0.92, 0.38)});
            skEllipse(sketch, "E5.9.0.7", {"center": v(12.26, -8.6) * mm, "majorRadius": 0.25 * mm, "minorRadius": 0.25 * mm, "majorAxis": v(0.92, 0.38)});
            skEllipse(sketch, "E5.9.0.8", {"center": v(11.46, -8.6) * mm, "majorRadius": 0.25 * mm, "minorRadius": 0.25 * mm, "majorAxis": v(0.92, 0.38)});
            skEllipse(sketch, "E5.9.0.9", {"center": v(10.66, -8.6) * mm, "majorRadius": 0.25 * mm, "minorRadius": 0.25 * mm, "majorAxis": v(0.92, 0.38)});
            skEllipse(sketch, "E5.9.0.10", {"center": v(9.86, -8.6) * mm, "majorRadius": 0.25 * mm, "minorRadius": 0.25 * mm, "majorAxis": v(0.92, 0.38)});
            skEllipse(sketch, "E5.9.0.11", {"center": v(9.06, -8.6) * mm, "majorRadius": 0.25 * mm, "minorRadius": 0.25 * mm, "majorAxis": v(0.92, 0.38)});
            skEllipse(sketch, "E5.9.0.12", {"center": v(8.26, -8.6) * mm, "majorRadius": 0.25 * mm, "minorRadius": 0.25 * mm, "majorAxis": v(0.92, 0.38)});
            skEllipse(sketch, "E5.9.0.13", {"center": v(7.46, -8.6) * mm, "majorRadius": 0.25 * mm, "minorRadius": 0.25 * mm, "majorAxis": v(0.92, 0.38)});
            skEllipse(sketch, "E5.9.0.14", {"center": v(6.66, -8.6) * mm, "majorRadius": 0.25 * mm, "minorRadius": 0.25 * mm, "majorAxis": v(0.92, 0.38)});
            skEllipse(sketch, "E5.9.0.15", {"center": v(5.06, -8.6) * mm, "majorRadius": 0.25 * mm, "minorRadius": 0.25 * mm, "majorAxis": v(0.92, 0.38)});
            skEllipse(sketch, "E5.9.0.16", {"center": v(4.26, -8.6) * mm, "majorRadius": 0.25 * mm, "minorRadius": 0.25 * mm, "majorAxis": v(0.92, 0.38)});
            skEllipse(sketch, "E5.9.0.17", {"center": v(5.86, -8.6) * mm, "majorRadius": 0.25 * mm, "minorRadius": 0.25 * mm, "majorAxis": v(0.92, 0.38)});
            skEllipse(sketch, "E5.9.0.18", {"center": v(3.46, -8.6) * mm, "majorRadius": 0.25 * mm, "minorRadius": 0.25 * mm, "majorAxis": v(0.92, 0.38)});
            skEllipse(sketch, "E5.9.0.19", {"center": v(2.66, -8.6) * mm, "majorRadius": 0.25 * mm, "minorRadius": 0.25 * mm, "majorAxis": v(0.92, 0.38)});
            skEllipse(sketch, "E5.9.0.20", {"center": v(1.86, -8.6) * mm, "majorRadius": 0.25 * mm, "minorRadius": 0.25 * mm, "majorAxis": v(0.92, 0.38)});
            skLineSegment(sketch, "E5.direction1", {"start": v(18.1, -1.4) * mm, "end": v(18.07, -2.2) * mm, "construction": true});
            skSolve(sketch);
        }
        {
            var Q0;
            Q0=makeQuery(id+"F0.imprint","IMPRINT",FACE,{"disambiguationData":[TD([[makeQuery(id+"F0.imprint","IMPRINT",EDGE,{"derivedFrom":sQuery(id+"F0.wireOp",EDGE,"E0.bottom")}),-1.0]])]});
            extrude(context, id + "F1", {"entities" : qUnion([Q0]), "depth" : 0.2 * mm, "offsetDistance" : 25.4 * mm});
        }
    });
